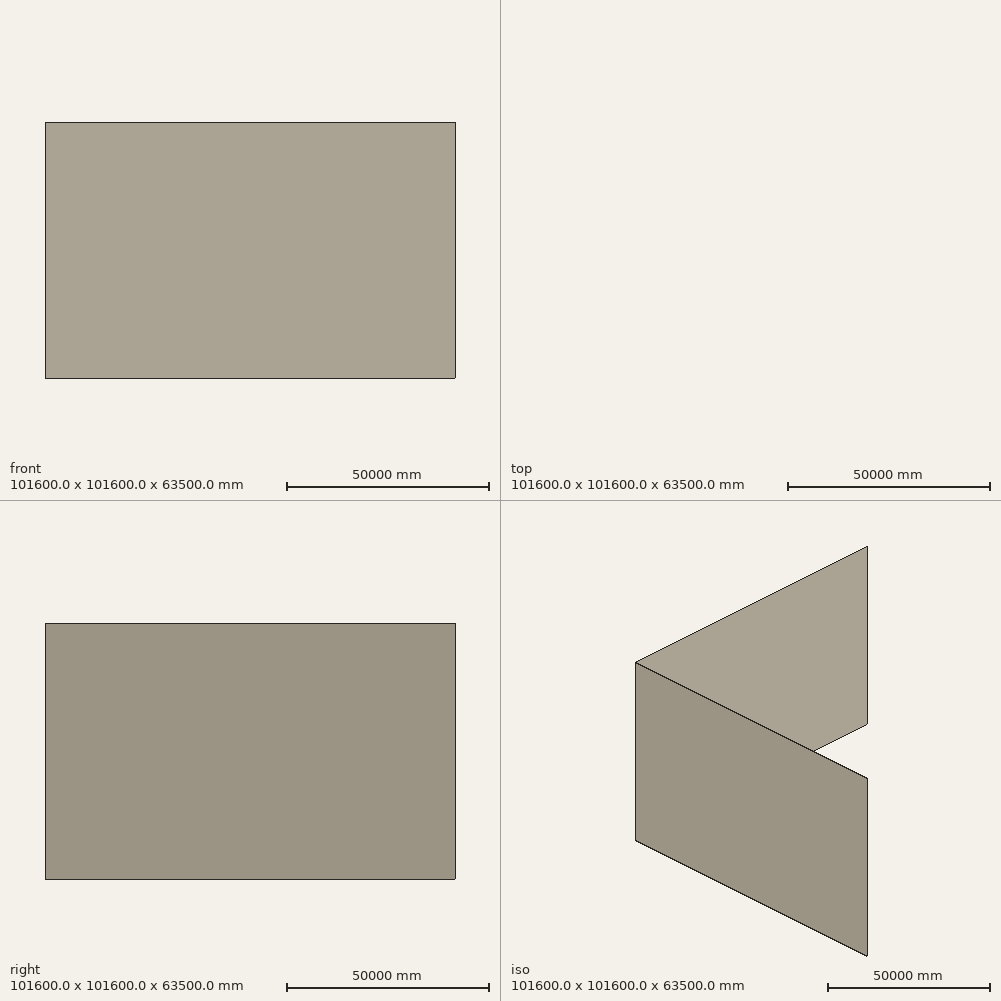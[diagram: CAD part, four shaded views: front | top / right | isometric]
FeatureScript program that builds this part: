
annotation { "Feature Type Name" : "Feature", "Feature Type Description" : "" }
export const myFeature = defineFeature(function(context is Context, id is Id, definition is map)
    precondition{}
    {
        {
            var Q0;
            Q0=qCreatedBy(makeId("Top.planeOp"),FACE);
            var sketch = newSketch(context, id + "F0", { "sketchPlane" : qUnion([Q0])});
            skLineSegment(sketch, "E0", {"start": v(-50800, -61078.2) * mm, "end": v(-50800, 40521.8) * mm});
            skLineSegment(sketch, "E1", {"start": v(-50800, 40521.8) * mm, "end": v(50800, 40521.8) * mm});
            skPoint(sketch, "E2", {"position": v(0, 40521.8) * mm});
            skSolve(sketch);
        }
        {
            var Q0;
            Q0 = qSketchRegion(id + "F0", true);
            var Q1;
            Q1=sQuery(id+"F0.wireOp",EDGE,"E0");
            var Q2;
            Q2=sQuery(id+"F0.wireOp",EDGE,"E1");
            extrude(context, id + "F1", {"entities" : qUnion([Q0]), "bodyType" : ToolBodyType.SURFACE, "surfaceEntities" : qUnion([Q1, Q2]), "depth" : 63500 * mm, "offsetDistance" : 25.4 * mm});
        }
    });
